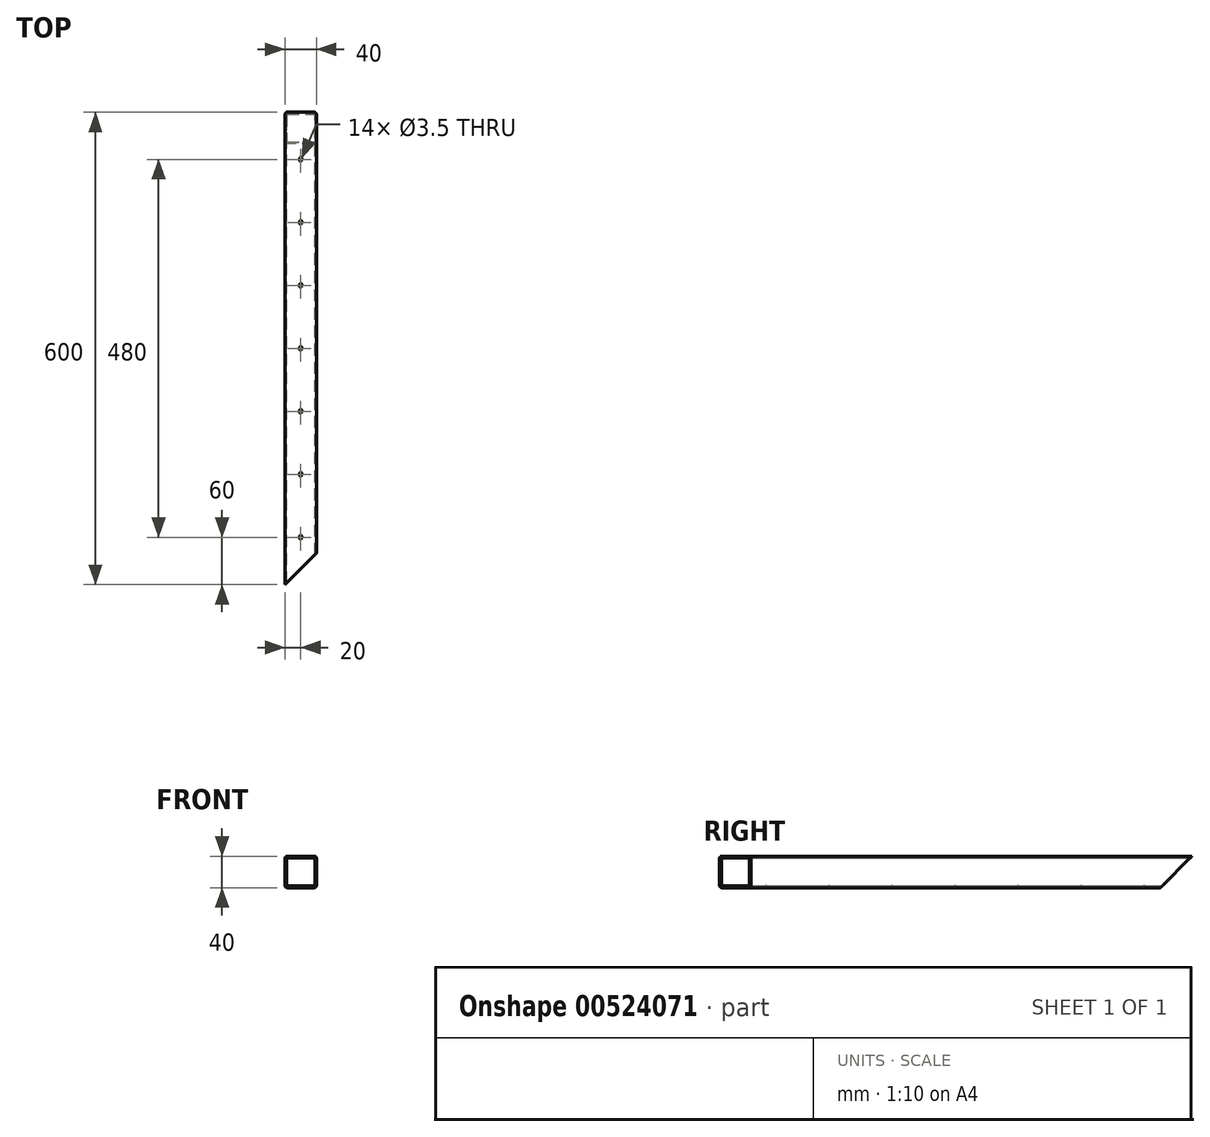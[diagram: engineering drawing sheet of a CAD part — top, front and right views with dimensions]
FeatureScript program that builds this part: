
annotation { "Feature Type Name" : "Feature", "Feature Type Description" : "" }
export const myFeature = defineFeature(function(context is Context, id is Id, definition is map)
    precondition{}
    {
        {
            assignVariable(context, id + "F0", {"name" : "R", "anyValue" : 3});
        }
        {
            assignVariable(context, id + "F1", {"name" : "W", "anyValue" : 2});
        }
        {
            var Q0;
            Q0=qCreatedBy(makeId("Front.planeOp"),FACE);
            var sketch = newSketch(context, id + "F2", { "sketchPlane" : qUnion([Q0])});
            skLineSegment(sketch, "E0.bottom", {"start": v(-20, 20) * mm, "end": v(20, 20) * mm});
            skLineSegment(sketch, "E0.top", {"start": v(-20, -20) * mm, "end": v(20, -20) * mm});
            skLineSegment(sketch, "E0.left", {"start": v(-20, 20) * mm, "end": v(-20, -20) * mm});
            skLineSegment(sketch, "E0.right", {"start": v(20, 20) * mm, "end": v(20, -20) * mm});
            skSolve(sketch);
        }
        {
            var Q0;
            Q0=qSketchRegion(id+"F2",true);
            extrude(context, id + "F3", {"entities" : qUnion([Q0]), "endBound" : BoundingType.SYMMETRIC, "depth" : 600 * mm, "offsetDistance" : 25 * mm});
        }
        {
            var Q0;
            Q0=makeQuery(id+"F3.opExtrude","SWEPT_EDGE",EDGE,{"disambiguationData":[OSD([sQuery(id+"F2.wireOp",EDGE,"E0.bottom"),sQuery(id+"F2.wireOp",EDGE,"E0.right")])]});
            var Q1;
            Q1=makeQuery(id+"F3.opExtrude","SWEPT_EDGE",EDGE,{"disambiguationData":[OSD([sQuery(id+"F2.wireOp",EDGE,"E0.bottom"),sQuery(id+"F2.wireOp",EDGE,"E0.left")])]});
            var Q2;
            Q2=makeQuery(id+"F3.opExtrude","SWEPT_EDGE",EDGE,{"disambiguationData":[OSD([sQuery(id+"F2.wireOp",EDGE,"E0.top"),sQuery(id+"F2.wireOp",EDGE,"E0.right")])]});
            var Q3;
            Q3=makeQuery(id+"F3.opExtrude","SWEPT_EDGE",EDGE,{"disambiguationData":[OSD([sQuery(id+"F2.wireOp",EDGE,"E0.top"),sQuery(id+"F2.wireOp",EDGE,"E0.left")])]});
            fillet(context, id + "F4", {"entities" : qUnion([Q0, Q1, Q2, Q3]), "radius" : (getVariable(context, 'R')) * mm, "tangentPropagation" : true, "allowEdgeOverflow" : false});
        }
        {
            var Q0;
            Q0=makeQuery(id+"F3.opExtrude","CAP_FACE",FACE,{"disambiguationData":[OSD([sQuery(id+"F2.wireOp",EDGE,"E0.bottom"),sQuery(id+"F2.wireOp",EDGE,"E0.top"),sQuery(id+"F2.wireOp",EDGE,"E0.left"),sQuery(id+"F2.wireOp",EDGE,"E0.right")])],"isStart":false});
            var Q1;
            Q1=makeQuery(id+"F3.opExtrude","CAP_FACE",FACE,{"disambiguationData":[OSD([sQuery(id+"F2.wireOp",EDGE,"E0.bottom"),sQuery(id+"F2.wireOp",EDGE,"E0.top"),sQuery(id+"F2.wireOp",EDGE,"E0.left"),sQuery(id+"F2.wireOp",EDGE,"E0.right")])],"isStart":true});
            shell(context, id + "F5", {"entities" : qUnion([Q0, Q1]), "thickness" : (getVariable(context, 'W')) * mm});
        }
        {
            var Q0;
            Q0=makeQuery(id+"F3.opExtrude","SWEPT_FACE",FACE,{"disambiguationData":[OSD([sQuery(id+"F2.wireOp",EDGE,"E0.left")])]});
            var sketch = newSketch(context, id + "F6", { "sketchPlane" : qUnion([Q0])});
            skLineSegment(sketch, "E1", {"start": v(-300, -20) * mm, "end": v(-260, -20) * mm});
            skLineSegment(sketch, "E2", {"start": v(-260, -20) * mm, "end": v(-300, 20) * mm});
            skLineSegment(sketch, "E3", {"start": v(-300, 20) * mm, "end": v(-300, -20) * mm});
            skSolve(sketch);
        }
        {
            var Q0;
            Q0 = qSketchRegion(id + "F6", true);
            extrude(context, id + "F7", {"entities" : qUnion([Q0]), "operationType" : NewBodyOperationType.REMOVE, "endBound" : BoundingType.THROUGH_ALL, "oppositeDirection" : true, "depth" : 25 * mm, "offsetDistance" : 25 * mm});
        }
        {
            var Q0;
            Q0=makeQuery(id+"F3.opExtrude","SWEPT_FACE",FACE,{"disambiguationData":[OSD([sQuery(id+"F2.wireOp",EDGE,"E0.bottom")])]});
            var sketch = newSketch(context, id + "F8", { "sketchPlane" : qUnion([Q0])});
            skLineSegment(sketch, "E4.0", {"start": v(20, 297) * mm, "end": v(20, -300) * mm, "construction": true});
            skLineSegment(sketch, "E5", {"start": v(20, -260) * mm, "end": v(-20, -300) * mm});
            skLineSegment(sketch, "E6", {"start": v(-20, -300) * mm, "end": v(20, -300) * mm});
            skLineSegment(sketch, "E7", {"start": v(20, -260) * mm, "end": v(20, -300) * mm});
            skSolve(sketch);
        }
        {
            var Q0;
            Q0 = qSketchRegion(id + "F8", true);
            extrude(context, id + "F9", {"entities" : qUnion([Q0]), "operationType" : NewBodyOperationType.REMOVE, "endBound" : BoundingType.THROUGH_ALL, "oppositeDirection" : true, "depth" : 25 * mm, "offsetDistance" : 25 * mm});
        }
        {
            var Q0;
            Q0=makeQuery(id+"F3.opExtrude","SWEPT_FACE",FACE,{"disambiguationData":[OSD([sQuery(id+"F2.wireOp",EDGE,"E0.top")])]});
            var sketch = newSketch(context, id + "F10", { "sketchPlane" : qUnion([Q0])});
            skPoint(sketch, "E8", {"position": v(0, 240) * mm});
            skPoint(sketch, "E9", {"position": v(0, 160) * mm});
            skPoint(sketch, "E10", {"position": v(0, 80) * mm});
            skPoint(sketch, "E11", {"position": v(0, 0) * mm});
            skPoint(sketch, "E12", {"position": v(0, -80) * mm});
            skPoint(sketch, "E13", {"position": v(0, -160) * mm});
            skPoint(sketch, "E14", {"position": v(0, -240) * mm});
            skSolve(sketch);
        }
        {
            var Q0;
            Q0=sQuery(id+"F10.wireOp",VERTEX,"E8");
            var Q1;
            Q1=sQuery(id+"F10.wireOp",VERTEX,"E9");
            var Q2;
            Q2=sQuery(id+"F10.wireOp",VERTEX,"E10");
            var Q3;
            Q3=sQuery(id+"F10.wireOp",VERTEX,"E11");
            var Q4;
            Q4=sQuery(id+"F10.wireOp",VERTEX,"E12");
            var Q5;
            Q5=sQuery(id+"F10.wireOp",VERTEX,"E13");
            var Q6;
            Q6=sQuery(id+"F10.wireOp",VERTEX,"E14");
            var Q7;
            Q7=makeQuery(id+"F3.opExtrude","SWEPT_BODY",BODY,{"disambiguationData":[OSD([sQuery(id+"F2.wireOp",EDGE,"E0.bottom"),sQuery(id+"F2.wireOp",EDGE,"E0.top"),sQuery(id+"F2.wireOp",EDGE,"E0.left"),sQuery(id+"F2.wireOp",EDGE,"E0.right")])]});
            hole(context, id + "F11", {"style" : HoleStyle.C_SINK, "endStyle" : HoleEndStyle.THROUGH, "holeDiameter" : 3.5 * mm, "cSinkDiameter" : 6 * mm, "cSinkAngle" : 90 * degree, "isTappedThrough" : true, "tappedDepth" : 12 * mm, "tapClearance" : 3, "locations" : qUnion([Q0, Q1, Q2, Q3, Q4, Q5, Q6]), "scope" : qUnion([Q7])});
        }
    });
